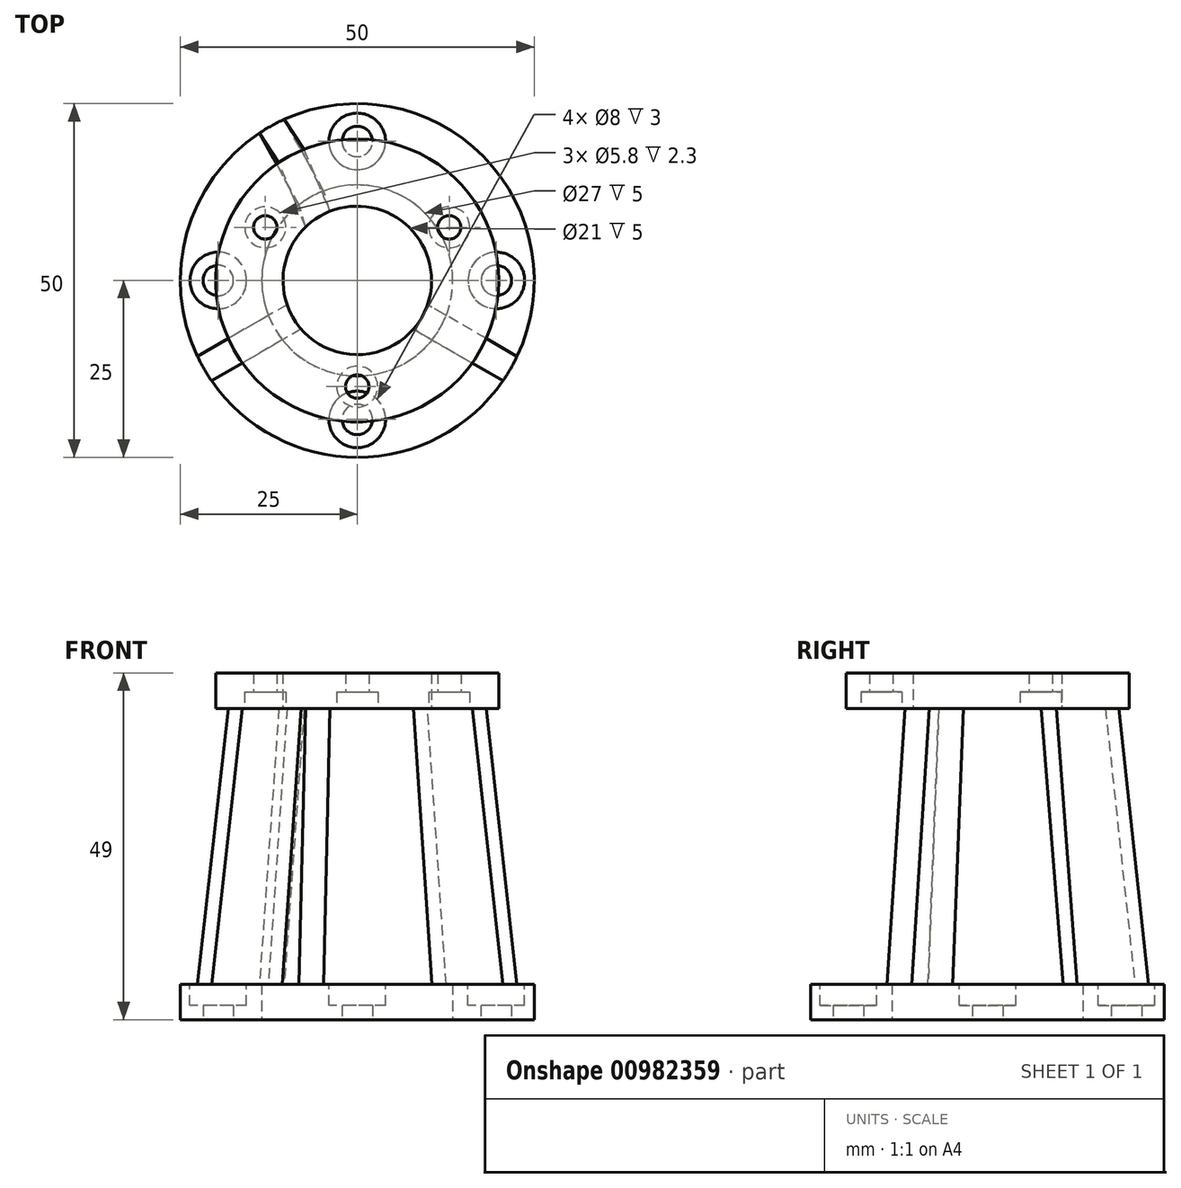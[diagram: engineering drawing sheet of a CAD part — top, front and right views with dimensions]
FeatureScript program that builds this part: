
annotation { "Feature Type Name" : "Feature", "Feature Type Description" : "" }
export const myFeature = defineFeature(function(context is Context, id is Id, definition is map)
    precondition{}
    {
        {
            var Q0;
            Q0=qCreatedBy(makeId("Top.planeOp"),FACE);
            var sketch = newSketch(context, id + "F0", { "sketchPlane" : qUnion([Q0])});
            skCircle(sketch, "E0", {"center": v(0, 0) * mm, "radius": 25 * mm});
            skCircle(sketch, "E1", {"center": v(0, 0) * mm, "radius": 13.5 * mm});
            skCircle(sketch, "E2", {"center": v(19.65, 0) * mm, "radius": 2.15 * mm});
            skCircle(sketch, "E3", {"center": v(-19.65, 0) * mm, "radius": 2.15 * mm});
            skCircle(sketch, "E4", {"center": v(0, 19.65) * mm, "radius": 2.15 * mm});
            skCircle(sketch, "E5", {"center": v(0, -19.65) * mm, "radius": 2.15 * mm});
            skLineSegment(sketch, "E6", {"start": v(-19.65, 0) * mm, "end": v(0, 0) * mm, "construction": true});
            skLineSegment(sketch, "E7", {"start": v(0, 0) * mm, "end": v(0, 19.65) * mm, "construction": true});
            skLineSegment(sketch, "E8", {"start": v(0, 0) * mm, "end": v(19.65, 0) * mm, "construction": true});
            skLineSegment(sketch, "E9", {"start": v(0, 0) * mm, "end": v(0, -19.65) * mm, "construction": true});
            skSolve(sketch);
        }
        {
            var Q0;
            Q0 = qSketchRegion(id + "F0", true);
            extrude(context, id + "F1", {"entities" : qUnion([Q0]), "depth" : 5 * mm, "offsetDistance" : 25 * mm});
        }
        {
            var Q0;
            Q0=makeQuery(id+"F1.opExtrude","CAP_FACE",FACE,{"disambiguationData":[OSD([sQuery(id+"F0.wireOp",EDGE,"E0"),sQuery(id+"F0.wireOp",EDGE,"E1"),sQuery(id+"F0.wireOp",EDGE,"E2"),sQuery(id+"F0.wireOp",EDGE,"E3"),sQuery(id+"F0.wireOp",EDGE,"E4"),sQuery(id+"F0.wireOp",EDGE,"E5")])],"isStart":false});
            var sketch = newSketch(context, id + "F2", { "sketchPlane" : qUnion([Q0])});
            skCircle(sketch, "E10", {"center": v(0, -19.65) * mm, "radius": 4 * mm});
            skCircle(sketch, "E11", {"center": v(19.65, 0) * mm, "radius": 4 * mm});
            skCircle(sketch, "E12", {"center": v(0, 19.65) * mm, "radius": 4 * mm});
            skCircle(sketch, "E13", {"center": v(-19.65, 0) * mm, "radius": 4 * mm});
            skSolve(sketch);
        }
        {
            var Q0;
            Q0 = qSketchRegion(id + "F2", true);
            extrude(context, id + "F3", {"entities" : qUnion([Q0]), "operationType" : NewBodyOperationType.REMOVE, "oppositeDirection" : true, "depth" : 3 * mm, "offsetDistance" : 25 * mm});
        }
        {
            var Q0;
            Q0=makeQuery(id+"F1.opExtrude","CAP_FACE",FACE,{"disambiguationData":[OSD([sQuery(id+"F0.wireOp",EDGE,"E0"),sQuery(id+"F0.wireOp",EDGE,"E1"),sQuery(id+"F0.wireOp",EDGE,"E2"),sQuery(id+"F0.wireOp",EDGE,"E3"),sQuery(id+"F0.wireOp",EDGE,"E4"),sQuery(id+"F0.wireOp",EDGE,"E5")])],"isStart":false});
            cPlane(context, id + "F4", {"entities" : qUnion([Q0]), "cplaneType" : CPlaneType.OFFSET, "offset" : 39 * mm, "width" : 150 * mm, "height" : 150 * mm});
        }
        {
            var Q0;
            Q0=qCreatedBy(id+"F4.planeOp",FACE);
            var sketch = newSketch(context, id + "F5", { "sketchPlane" : qUnion([Q0])});
            skCircle(sketch, "E14", {"center": v(0, 0) * mm, "radius": 10.5 * mm});
            skCircle(sketch, "E15", {"center": v(0, 0) * mm, "radius": 20 * mm});
            skCircle(sketch, "E16", {"center": v(0, -15.01) * mm, "radius": 1.65 * mm});
            skLineSegment(sketch, "E17", {"start": v(0, -15.01) * mm, "end": v(0, 0) * mm, "construction": true});
            skLineSegment(sketch, "E18", {"start": v(0, 0) * mm, "end": v(13, 7.5) * mm, "construction": true});
            skLineSegment(sketch, "E19", {"start": v(13, 7.5) * mm, "end": v(0, 0) * mm, "construction": true});
            skLineSegment(sketch, "E20", {"start": v(0, 0) * mm, "end": v(-13, 7.5) * mm, "construction": true});
            skCircle(sketch, "E21", {"center": v(13, 7.5) * mm, "radius": 1.65 * mm});
            skCircle(sketch, "E22", {"center": v(-13, 7.5) * mm, "radius": 1.65 * mm});
            skLineSegment(sketch, "E23", {"start": v(13, 7.5) * mm, "end": v(0, -15.01) * mm, "construction": true});
            skSolve(sketch);
        }
        {
            var Q0;
            Q0 = qSketchRegion(id + "F5", true);
            extrude(context, id + "F6", {"entities" : qUnion([Q0]), "depth" : 5 * mm, "offsetDistance" : 25 * mm});
        }
        {
            var Q0;
            Q0=makeQuery(id+"F6.opExtrude","CAP_FACE",FACE,{"disambiguationData":[OSD([sQuery(id+"F5.wireOp",EDGE,"E14"),sQuery(id+"F5.wireOp",EDGE,"E15"),sQuery(id+"F5.wireOp",EDGE,"E16"),sQuery(id+"F5.wireOp",EDGE,"E21"),sQuery(id+"F5.wireOp",EDGE,"E22")])],"isStart":true});
            var sketch = newSketch(context, id + "F7", { "sketchPlane" : qUnion([Q0])});
            skCircle(sketch, "E24", {"center": v(-13, -7.5) * mm, "radius": 2.9 * mm});
            skCircle(sketch, "E25", {"center": v(0, 15.01) * mm, "radius": 2.9 * mm});
            skCircle(sketch, "E26", {"center": v(13, -7.5) * mm, "radius": 2.9 * mm});
            skSolve(sketch);
        }
        {
            var Q0;
            Q0 = qSketchRegion(id + "F7", true);
            extrude(context, id + "F8", {"entities" : qUnion([Q0]), "operationType" : NewBodyOperationType.REMOVE, "oppositeDirection" : true, "depth" : 2.3 * mm, "offsetDistance" : 25 * mm});
        }
        {
            var Q0;
            Q0=makeQuery(id+"F6.opExtrude","CAP_FACE",FACE,{"disambiguationData":[OSD([sQuery(id+"F5.wireOp",EDGE,"E14"),sQuery(id+"F5.wireOp",EDGE,"E15"),sQuery(id+"F5.wireOp",EDGE,"E16"),sQuery(id+"F5.wireOp",EDGE,"E21"),sQuery(id+"F5.wireOp",EDGE,"E22")])],"isStart":true});
            var sketch = newSketch(context, id + "F9", { "sketchPlane" : qUnion([Q0])});
            skLineSegment(sketch, "E27", {"start": v(0, 0) * mm, "end": v(-17.32, 10) * mm, "construction": true});
            skLineSegment(sketch, "E28", {"start": v(0, 0) * mm, "end": v(17.32, 10) * mm, "construction": true});
            skLineSegment(sketch, "E29", {"start": v(0, 0) * mm, "end": v(0, -20) * mm, "construction": true});
            skLineSegment(sketch, "E30", {"start": v(-13, -7.5) * mm, "end": v(-17.32, 10) * mm, "construction": true});
            skLineSegment(sketch, "E31", {"start": v(0, 15.01) * mm, "end": v(-17.32, 10) * mm, "construction": true});
            skLineSegment(sketch, "E32", {"start": v(18.23, 8.22) * mm, "end": v(9.93, 3.42) * mm});
            skLineSegment(sketch, "E33", {"start": v(7.93, 6.89) * mm, "end": v(16.23, 11.68) * mm});
            skLineSegment(sketch, "E34", {"start": v(2, -19.9) * mm, "end": v(2, -10.3) * mm});
            skLineSegment(sketch, "E35", {"start": v(-2, -10.3) * mm, "end": v(-2, -19.9) * mm});
            skLineSegment(sketch, "E36", {"start": v(-7.93, 6.89) * mm, "end": v(-16.23, 11.68) * mm});
            skLineSegment(sketch, "E37", {"start": v(-9.93, 3.42) * mm, "end": v(-18.23, 8.22) * mm});
            skLineSegment(sketch, "E38", {"start": v(-7.29, -7.56) * mm, "end": v(-11.07, -16.65) * mm});
            skLineSegment(sketch, "E39", {"start": v(-7.52, -18.53) * mm, "end": v(-3.87, -9.76) * mm});
            skLineSegment(sketch, "E40", {"start": v(3.87, -9.76) * mm, "end": v(7.52, -18.53) * mm});
            skLineSegment(sketch, "E41", {"start": v(11.07, -16.65) * mm, "end": v(7.29, -7.56) * mm});
            skLineSegment(sketch, "E42", {"start": v(-7.29, -7.56) * mm, "end": v(0, -10.5) * mm, "construction": true});
            skLineSegment(sketch, "E43", {"start": v(0, -10.5) * mm, "end": v(7.29, -7.56) * mm, "construction": true});
            skLineSegment(sketch, "E44", {"start": v(-7.52, -18.53) * mm, "end": v(0, -20) * mm, "construction": true});
            skLineSegment(sketch, "E45", {"start": v(7.52, -18.53) * mm, "end": v(0, -20) * mm, "construction": true});
            skSolve(sketch);
        }
        {
            var Q0;
            Q0=makeQuery(id+"F1.opExtrude","CAP_FACE",FACE,{"disambiguationData":[OSD([sQuery(id+"F0.wireOp",EDGE,"E0"),sQuery(id+"F0.wireOp",EDGE,"E1"),sQuery(id+"F0.wireOp",EDGE,"E2"),sQuery(id+"F0.wireOp",EDGE,"E3"),sQuery(id+"F0.wireOp",EDGE,"E4"),sQuery(id+"F0.wireOp",EDGE,"E5")])],"isStart":false});
            var sketch = newSketch(context, id + "F10", { "sketchPlane" : qUnion([Q0])});
            skLineSegment(sketch, "E46", {"start": v(-12.56, -4.94) * mm, "end": v(-22.58, -10.73) * mm});
            skLineSegment(sketch, "E47", {"start": v(-10.56, -8.4) * mm, "end": v(-20.58, -14.2) * mm});
            skLineSegment(sketch, "E48", {"start": v(10.56, -8.4) * mm, "end": v(20.58, -14.2) * mm});
            skLineSegment(sketch, "E49", {"start": v(22.58, -10.73) * mm, "end": v(12.56, -4.94) * mm});
            skLineSegment(sketch, "E50", {"start": v(0, 0) * mm, "end": v(12.12, 21.87) * mm, "construction": true});
            skLineSegment(sketch, "E51", {"start": v(0, 0) * mm, "end": v(-12.12, 21.87) * mm, "construction": true});
            skLineSegment(sketch, "E52", {"start": v(13.83, 20.83) * mm, "end": v(8.22, 10.7) * mm});
            skLineSegment(sketch, "E53", {"start": v(10.33, 22.77) * mm, "end": v(4.72, 12.65) * mm});
            skLineSegment(sketch, "E54", {"start": v(-4.72, 12.65) * mm, "end": v(-10.33, 22.77) * mm});
            skLineSegment(sketch, "E55", {"start": v(-8.22, 10.7) * mm, "end": v(-13.83, 20.83) * mm});
            skSolve(sketch);
        }
        {
            var Q1;
            {var subQ0=sQuery(id+"F10.wireOp",EDGE,"E48");Q1=makeQuery(id+"F10.imprint","IMPRINT",FACE,{"disambiguationData":[TD([[makeQuery(id+"F10.imprint","IMPRINT",EDGE,{"derivedFrom":subQ0}),1.0]])]});}
            var Q2;
            {var subQ0=sQuery(id+"F9.wireOp",EDGE,"E32");Q2=makeQuery(id+"F9.imprint","IMPRINT",FACE,{"disambiguationData":[TD([[makeQuery(id+"F9.imprint","IMPRINT",EDGE,{"derivedFrom":subQ0}),-1.0]])]});}
            loft(context, id + "F11", {"operationType" : NewBodyOperationType.ADD, "sheetProfilesArray" : [{ "sheetProfileEntities" : qUnion([Q1]) }, { "sheetProfileEntities" : qUnion([Q2]) }]});
        }
        {
            var Q1;
            {var subQ0=sQuery(id+"F9.wireOp",EDGE,"E36");Q1=makeQuery(id+"F9.imprint","IMPRINT",FACE,{"disambiguationData":[TD([[makeQuery(id+"F9.imprint","IMPRINT",EDGE,{"derivedFrom":subQ0}),1.0]])]});}
            var Q2;
            {var subQ0=sQuery(id+"F10.wireOp",EDGE,"E46");Q2=makeQuery(id+"F10.imprint","IMPRINT",FACE,{"disambiguationData":[TD([[makeQuery(id+"F10.imprint","IMPRINT",EDGE,{"derivedFrom":subQ0}),1.0]])]});}
            loft(context, id + "F12", {"operationType" : NewBodyOperationType.ADD, "sheetProfilesArray" : [{ "sheetProfileEntities" : qUnion([Q1]) }, { "sheetProfileEntities" : qUnion([Q2]) }]});
        }
        {
            var Q1;
            {var subQ0=sQuery(id+"F9.wireOp",EDGE,"E38");Q1=makeQuery(id+"F9.imprint","IMPRINT",FACE,{"disambiguationData":[TD([[makeQuery(id+"F9.imprint","IMPRINT",EDGE,{"derivedFrom":subQ0}),1.0]])]});}
            var Q2;
            {var subQ0=sQuery(id+"F10.wireOp",EDGE,"E54");Q2=makeQuery(id+"F10.imprint","IMPRINT",FACE,{"disambiguationData":[TD([[makeQuery(id+"F10.imprint","IMPRINT",EDGE,{"derivedFrom":subQ0}),1.0]])]});}
            loft(context, id + "F13", {"operationType" : NewBodyOperationType.ADD, "sheetProfilesArray" : [{ "sheetProfileEntities" : qUnion([Q1]) }, { "sheetProfileEntities" : qUnion([Q2]) }]});
        }
    });
